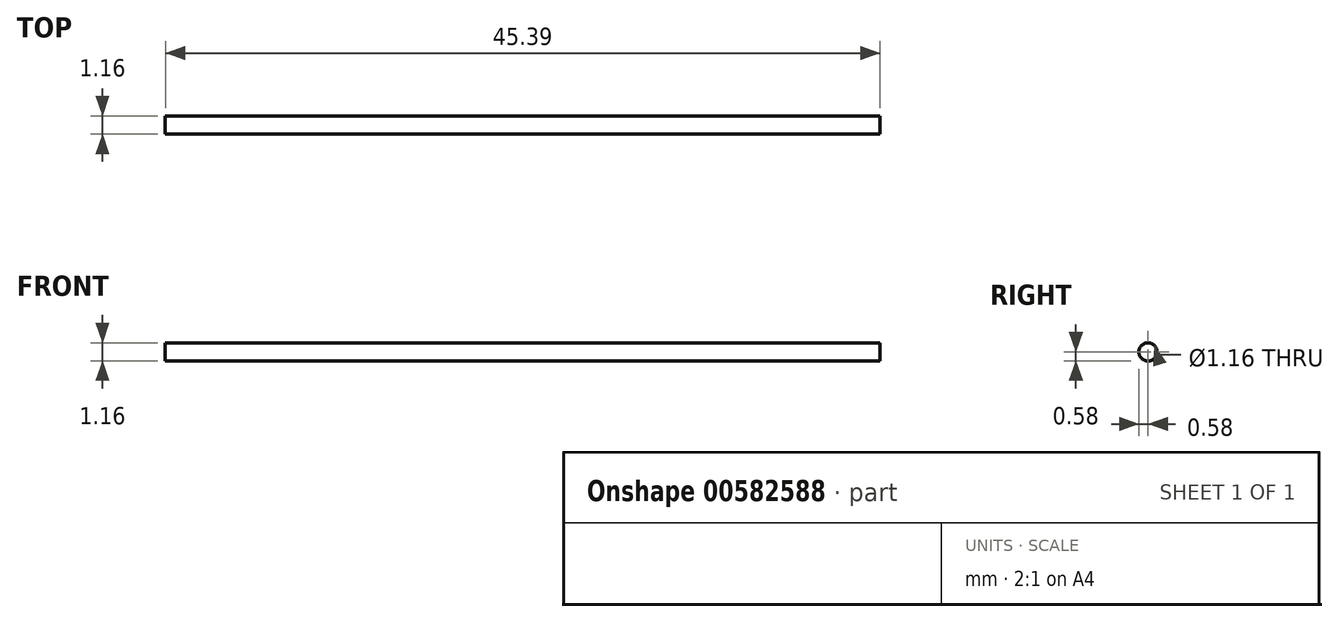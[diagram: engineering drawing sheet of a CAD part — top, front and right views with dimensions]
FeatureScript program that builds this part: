
annotation { "Feature Type Name" : "Feature", "Feature Type Description" : "" }
export const myFeature = defineFeature(function(context is Context, id is Id, definition is map)
    precondition{}
    {
        {
            var Q0;
            Q0=qCreatedBy(makeId("Front.planeOp"),FACE);
            var sketch = newSketch(context, id + "F0", { "sketchPlane" : qUnion([Q0])});
            skLineSegment(sketch, "E0", {"start": v(-45.4, 0) * mm, "end": v(0, 0) * mm});
            skLineSegment(sketch, "E1", {"start": v(-45.4, -0.58) * mm, "end": v(0, -0.58) * mm});
            skSolve(sketch);
        }
        {
            var Q0;
            Q0 = qSketchRegion(id + "F0", true);
            var Q1;
            Q1=sQuery(id+"F0.wireOp",EDGE,"E0");
            var Q2;
            Q2=sQuery(id+"F0.wireOp",EDGE,"E1");
            revolve(context, id + "F1", {"bodyType" : ToolBodyType.SURFACE, "entities" : qUnion([Q0]), "surfaceEntities" : qUnion([Q1]), "axis" : qUnion([Q2]), "revolveType" : RevolveType.FULL});
        }
    });
